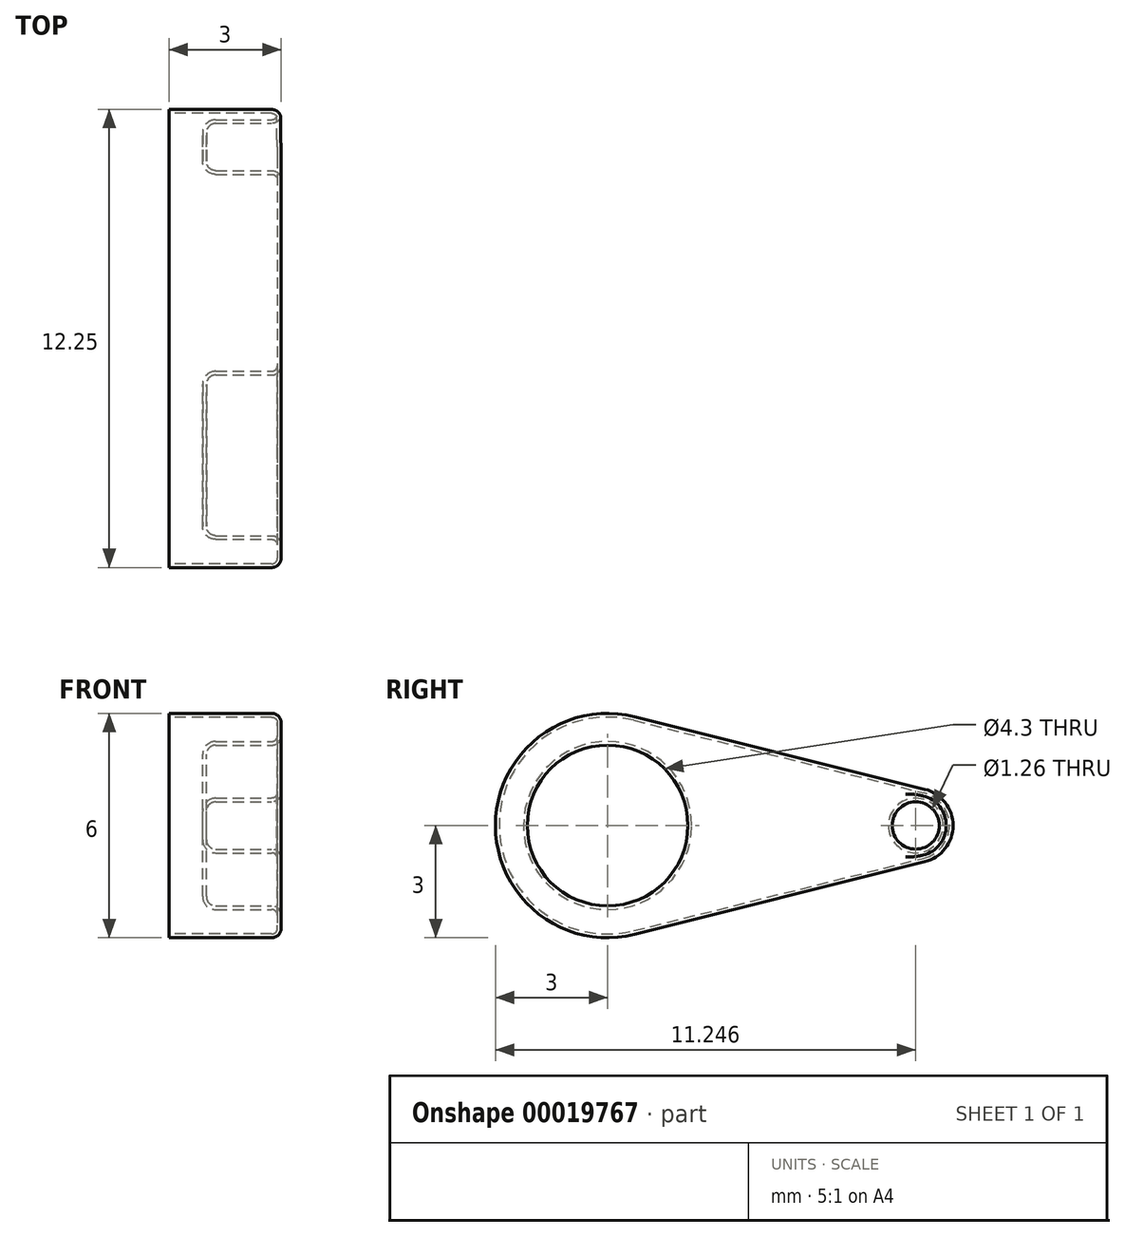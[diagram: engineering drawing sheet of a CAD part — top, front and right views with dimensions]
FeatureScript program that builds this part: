
annotation { "Feature Type Name" : "Feature", "Feature Type Description" : "" }
export const myFeature = defineFeature(function(context is Context, id is Id, definition is map)
    precondition{}
    {
        {
            var Q0;
            Q0=qCreatedBy(makeId("Right.planeOp"),FACE);
            var sketch = newSketch(context, id + "F0", { "sketchPlane" : qUnion([Q0])});
            skCircle(sketch, "E0", {"center": v(0, 0) * mm, "radius": 3 * mm});
            skCircle(sketch, "E1", {"center": v(8.25, 0) * mm, "radius": 1 * mm});
            skLineSegment(sketch, "E2", {"start": v(0.73, 2.91) * mm, "end": v(8.49, 0.97) * mm});
            skLineSegment(sketch, "E3", {"start": v(0.73, -2.91) * mm, "end": v(8.49, -0.97) * mm});
            skSolve(sketch);
        }
        {
            var Q0;
            {var subQ1=sQuery(id+"F0.wireOp",EDGE,"E2");Q0=makeQuery(id+"F0.imprint","IMPRINT",FACE,{"disambiguationData":[TD([[makeQuery(id+"F0.imprint","IMPRINT",EDGE,{"derivedFrom":subQ1}),-1.0]])]});}
            var Q1;
            {var subQ0=sQuery(id+"F0.wireOp",EDGE,"E1");var subQ2=makeQuery(id+"F0.imprint","INTERSECT",VERTEX,{"derivedFrom":[subQ0,sQuery(id+"F0.wireOp",EDGE,"E2")]});Q1=makeQuery(id+"F0.imprint","IMPRINT",FACE,{"disambiguationData":[TD([[makeQuery(id+"F0.imprint","IMPRINT",EDGE,{"disambiguationData":[TD([[subQ2,-1.0]])],"derivedFrom":subQ0}),1.0]])]});}
            var Q2;
            {var subQ0=sQuery(id+"F0.wireOp",EDGE,"E0");var subQ2=makeQuery(id+"F0.imprint","INTERSECT",VERTEX,{"derivedFrom":[subQ0,sQuery(id+"F0.wireOp",EDGE,"E2")]});Q2=makeQuery(id+"F0.imprint","IMPRINT",FACE,{"disambiguationData":[TD([[makeQuery(id+"F0.imprint","IMPRINT",EDGE,{"disambiguationData":[TD([[subQ2,-1.0]])],"derivedFrom":subQ0}),1.0]])]});}
            extrude(context, id + "F1", {"entities" : qUnion([Q0, Q1, Q2]), "depth" : 3 * mm});
        }
        {
            var Q0;
            Q0=makeQuery(id+"F1.opExtrude","CAP_FACE",FACE,{"disambiguationData":[OSD([sQuery(id+"F0.wireOp",EDGE,"E0"),sQuery(id+"F0.wireOp",EDGE,"E1"),sQuery(id+"F0.wireOp",EDGE,"E2"),sQuery(id+"F0.wireOp",EDGE,"E3")])],"isStart":false});
            var sketch = newSketch(context, id + "F2", { "sketchPlane" : qUnion([Q0])});
            skCircle(sketch, "E4", {"center": v(0, 0) * mm, "radius": 2.15 * mm});
            skCircle(sketch, "E5", {"center": v(8.25, 0) * mm, "radius": 0.63 * mm});
            skSolve(sketch);
        }
        {
            var Q0;
            Q0=makeQuery(id+"F2.imprint","IMPRINT",FACE,{"disambiguationData":[TD([[makeQuery(id+"F2.imprint","IMPRINT",EDGE,{"derivedFrom":sQuery(id+"F2.wireOp",EDGE,"E5")}),1.0]])]});
            var Q1;
            Q1=makeQuery(id+"F2.imprint","IMPRINT",FACE,{"disambiguationData":[TD([[makeQuery(id+"F2.imprint","IMPRINT",EDGE,{"derivedFrom":sQuery(id+"F2.wireOp",EDGE,"E4")}),1.0]])]});
            extrude(context, id + "F3", {"entities" : qUnion([Q0, Q1]), "operationType" : NewBodyOperationType.REMOVE, "oppositeDirection" : true, "depth" : 2 * mm});
        }
        {
            var Q0;
            Q0=makeQuery(id+"F3.boolean.opBoolean","COPY",FACE,{"derivedFrom":makeQuery(id+"F3.opExtrude","CAP_FACE",FACE,{"disambiguationData":[OSD([sQuery(id+"F2.wireOp",EDGE,"E4")])],"isStart":false})});
            var Q1;
            Q1=makeQuery(id+"F3.boolean.opBoolean","COPY",FACE,{"derivedFrom":makeQuery(id+"F3.opExtrude","CAP_FACE",FACE,{"disambiguationData":[OSD([sQuery(id+"F2.wireOp",EDGE,"E5")])],"isStart":false})});
            var Q2;
            Q2=makeQuery(id+"F1.opExtrude","CAP_FACE",FACE,{"disambiguationData":[OSD([sQuery(id+"F0.wireOp",EDGE,"E0"),sQuery(id+"F0.wireOp",EDGE,"E1"),sQuery(id+"F0.wireOp",EDGE,"E2"),sQuery(id+"F0.wireOp",EDGE,"E3")])],"isStart":false});
            fillet(context, id + "F4", {"entities" : qUnion([Q0, Q1, Q2]), "radius" : 0.25 * mm, "tangentPropagation" : true, "allowEdgeOverflow" : false});
        }
        {
            var Q0;
            Q0=makeQuery(id+"F1.opExtrude","CAP_FACE",FACE,{"disambiguationData":[OSD([sQuery(id+"F0.wireOp",EDGE,"E0"),sQuery(id+"F0.wireOp",EDGE,"E1"),sQuery(id+"F0.wireOp",EDGE,"E2"),sQuery(id+"F0.wireOp",EDGE,"E3")])],"isStart":true});
            shell(context, id + "F5", {"entities" : qUnion([Q0]), "thickness" : 0.1 * mm});
        }
    });
